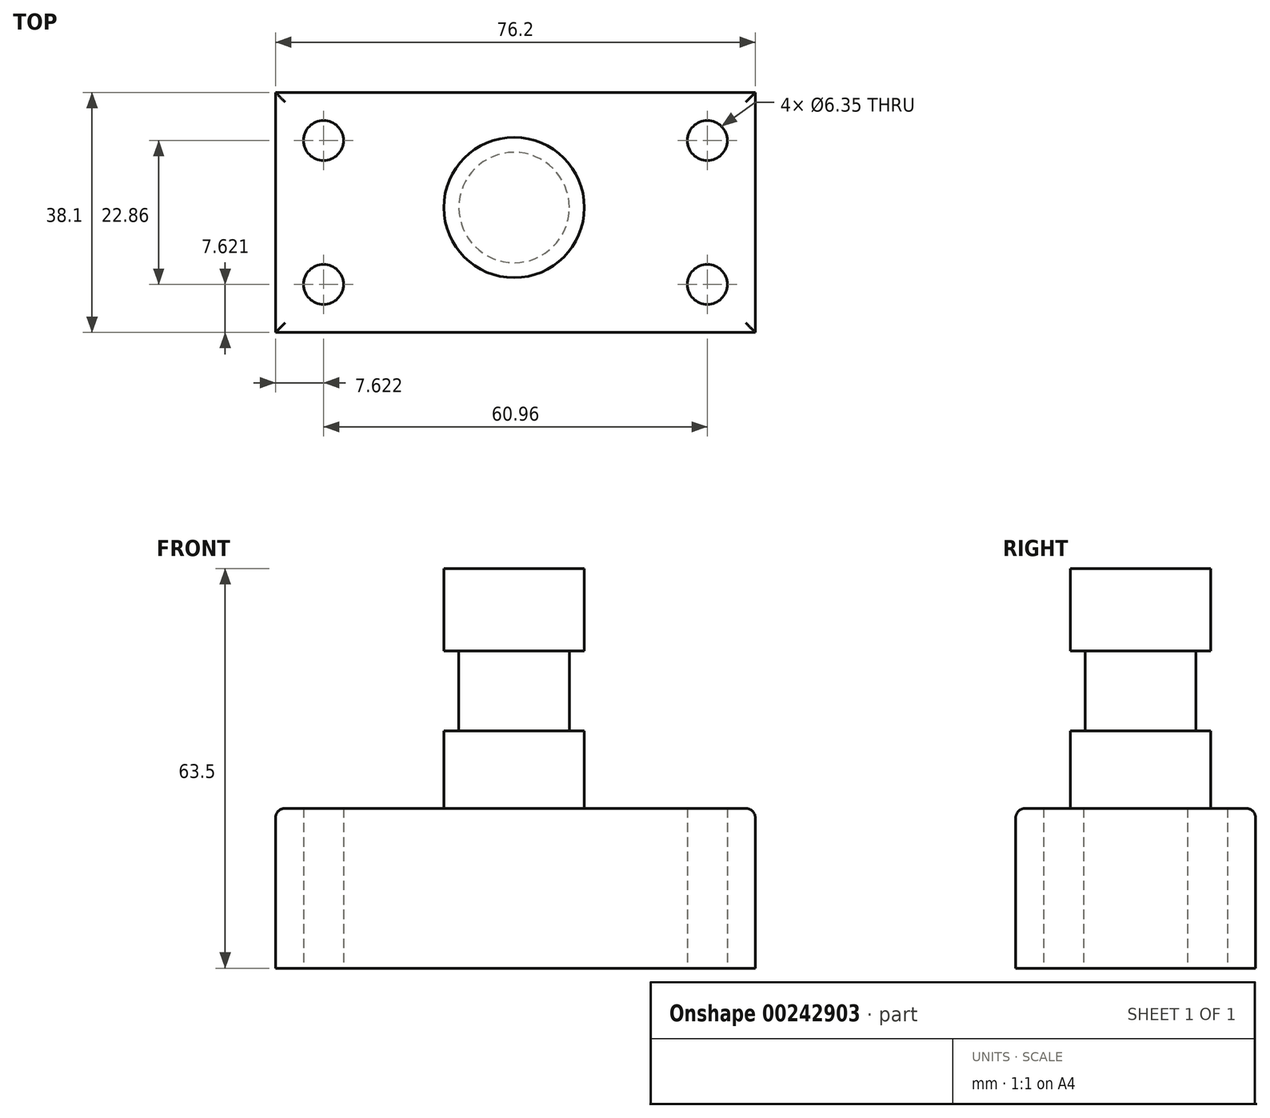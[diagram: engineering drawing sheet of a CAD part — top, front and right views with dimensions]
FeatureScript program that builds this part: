
annotation { "Feature Type Name" : "Feature", "Feature Type Description" : "" }
export const myFeature = defineFeature(function(context is Context, id is Id, definition is map)
    precondition{}
    {
        {
            var Q0;
            Q0=qCreatedBy(makeId("Top.planeOp"),FACE);
            var sketch = newSketch(context, id + "F0", { "sketchPlane" : qUnion([Q0])});
            skLineSegment(sketch, "E0.bottom", {"start": v(-37.89, 10.43) * mm, "end": v(38.31, 10.43) * mm});
            skLineSegment(sketch, "E0.top", {"start": v(-37.89, -27.67) * mm, "end": v(38.31, -27.67) * mm});
            skLineSegment(sketch, "E0.left", {"start": v(-37.89, 10.43) * mm, "end": v(-37.89, -27.67) * mm});
            skLineSegment(sketch, "E0.right", {"start": v(38.31, 10.43) * mm, "end": v(38.31, -27.67) * mm});
            skSolve(sketch);
        }
        {
            var Q0;
            Q0 = qSketchRegion(id + "F0", true);
            extrude(context, id + "F1", {"entities" : qUnion([Q0]), "depth" : 25.4 * mm});
        }
        {
            var Q0;
            Q0=qCreatedBy(makeId("Top.planeOp"),FACE);
            var sketch = newSketch(context, id + "F2", { "sketchPlane" : qUnion([Q0])});
            skCircle(sketch, "E1", {"center": v(-30.27, 2.81) * mm, "radius": 3.18 * mm});
            skCircle(sketch, "E2", {"center": v(-30.27, -20.05) * mm, "radius": 3.18 * mm});
            skCircle(sketch, "E3", {"center": v(30.7, 2.81) * mm, "radius": 3.18 * mm});
            skCircle(sketch, "E4", {"center": v(30.7, -20.05) * mm, "radius": 3.18 * mm});
            skSolve(sketch);
        }
        {
            var Q0;
            Q0 = qSketchRegion(id + "F2", true);
            extrude(context, id + "F3", {"entities" : qUnion([Q0]), "operationType" : NewBodyOperationType.REMOVE, "depth" : 25.4 * mm});
        }
        {
            var Q0;
            Q0=makeQuery(id+"F1.opExtrude","CAP_FACE",FACE,{"disambiguationData":[OSD([sQuery(id+"F0.wireOp",EDGE,"E0.bottom"),sQuery(id+"F0.wireOp",EDGE,"E0.top"),sQuery(id+"F0.wireOp",EDGE,"E0.left"),sQuery(id+"F0.wireOp",EDGE,"E0.right")])],"isStart":false});
            var sketch = newSketch(context, id + "F4", { "sketchPlane" : qUnion([Q0])});
            skCircle(sketch, "E5", {"center": v(0, -7.84) * mm, "radius": 11.15 * mm});
            skSolve(sketch);
        }
        {
            var Q0;
            Q0 = qSketchRegion(id + "F4", true);
            extrude(context, id + "F5", {"entities" : qUnion([Q0]), "operationType" : NewBodyOperationType.ADD, "depth" : 38.1 * mm});
        }
        {
            var Q0;
            Q0=qCreatedBy(makeId("Front.planeOp"),FACE);
            var sketch = newSketch(context, id + "F6", { "sketchPlane" : qUnion([Q0])});
            skLineSegment(sketch, "E6.bottom", {"start": v(-18.91, 50.4) * mm, "end": v(-3.93, 50.4) * mm});
            skLineSegment(sketch, "E6.top", {"start": v(-18.91, 37.7) * mm, "end": v(-3.93, 37.7) * mm});
            skLineSegment(sketch, "E6.left", {"start": v(-18.91, 50.4) * mm, "end": v(-18.91, 37.7) * mm});
            skLineSegment(sketch, "E6.right", {"start": v(-3.93, 50.4) * mm, "end": v(-3.93, 37.7) * mm});
            skSolve(sketch);
        }
        {
            var Q0;
            Q0=makeQuery(id+"F6.imprint","IMPRINT",FACE,{"disambiguationData":[TD([[makeQuery(id+"F6.imprint","IMPRINT",EDGE,{"derivedFrom":sQuery(id+"F6.wireOp",EDGE,"E6.bottom")}),-1.0]])]});
            var Q1;
            Q1=makeQuery(id+"F5.opExtrude","CAP_EDGE",EDGE,{"disambiguationData":[OSD([sQuery(id+"F4.wireOp",EDGE,"E5")])],"isStart":false});
            revolve(context, id + "F7", {"operationType" : NewBodyOperationType.REMOVE, "entities" : qUnion([Q0]), "axis" : qUnion([Q1]), "revolveType" : RevolveType.FULL, "oppositeDirection" : true});
        }
        {
            var Q0;
            Q0=makeQuery(id+"F1.opExtrude","CAP_EDGE",EDGE,{"disambiguationData":[OSD([sQuery(id+"F0.wireOp",EDGE,"E0.top")])],"isStart":false});
            var Q1;
            Q1=makeQuery(id+"F1.opExtrude","CAP_EDGE",EDGE,{"disambiguationData":[OSD([sQuery(id+"F0.wireOp",EDGE,"E0.left")])],"isStart":false});
            var Q2;
            Q2=makeQuery(id+"F1.opExtrude","CAP_EDGE",EDGE,{"disambiguationData":[OSD([sQuery(id+"F0.wireOp",EDGE,"E0.bottom")])],"isStart":false});
            var Q3;
            Q3=makeQuery(id+"F1.opExtrude","CAP_EDGE",EDGE,{"disambiguationData":[OSD([sQuery(id+"F0.wireOp",EDGE,"E0.right")])],"isStart":false});
            fillet(context, id + "F8", {"entities" : qUnion([Q0, Q1, Q2, Q3]), "radius" : 1.52 * mm, "tangentPropagation" : true, "allowEdgeOverflow" : false});
        }
    });
